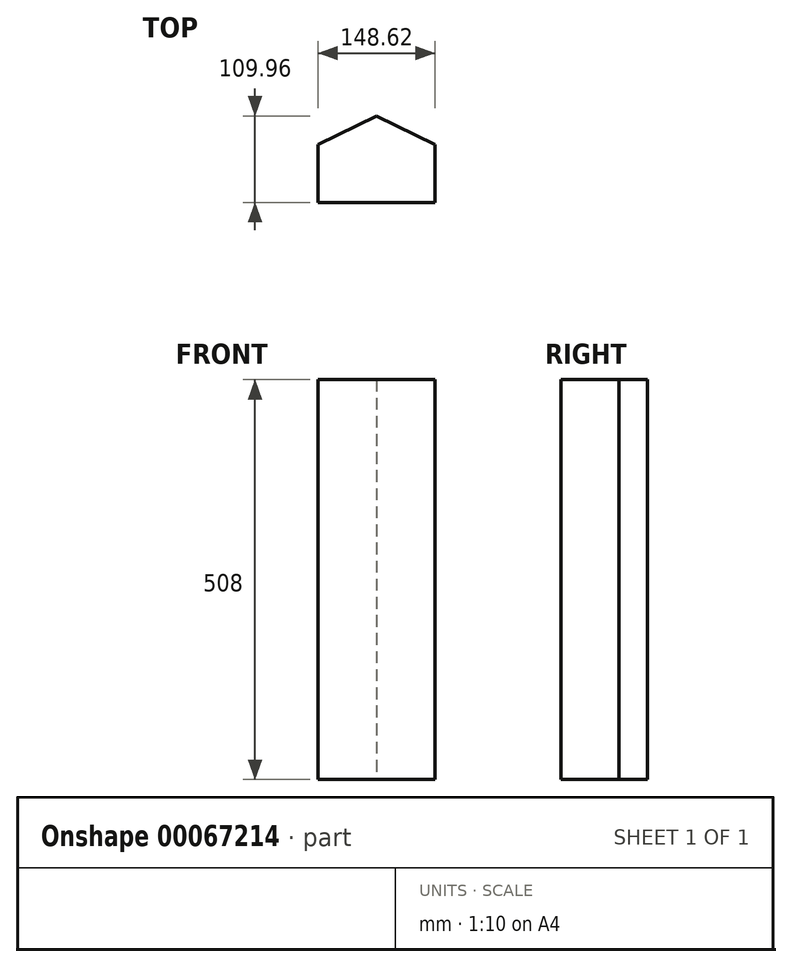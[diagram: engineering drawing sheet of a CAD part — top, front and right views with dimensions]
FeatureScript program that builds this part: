
annotation { "Feature Type Name" : "Feature", "Feature Type Description" : "" }
export const myFeature = defineFeature(function(context is Context, id is Id, definition is map)
    precondition{}
    {
        {
            var Q0;
            Q0=qCreatedBy(makeId("Top.planeOp"),FACE);
            var sketch = newSketch(context, id + "F0", { "sketchPlane" : qUnion([Q0])});
            skLineSegment(sketch, "E0.rect.bottom", {"start": v(0, -6) * mm, "end": v(0, -6) * mm});
            skLineSegment(sketch, "E0.rect.top", {"start": v(0, 6) * mm, "end": v(0, 6) * mm});
            skLineSegment(sketch, "E0.rect.left", {"start": v(0, -6) * mm, "end": v(0, 6) * mm});
            skLineSegment(sketch, "E0.rect.right", {"start": v(0, -6) * mm, "end": v(0, 6) * mm});
            skPoint(sketch, "E0.rect.middle", {"position": v(0, 0) * mm});
            skLineSegment(sketch, "E1.rect.bottom", {"start": v(-74.3, 36.85) * mm, "end": v(74.3, 36.85) * mm});
            skLineSegment(sketch, "E1.rect.top", {"start": v(-74.3, -36.85) * mm, "end": v(74.3, -36.85) * mm});
            skLineSegment(sketch, "E1.rect.left", {"start": v(-74.3, 36.85) * mm, "end": v(-74.3, -36.85) * mm});
            skLineSegment(sketch, "E1.rect.right", {"start": v(74.3, 36.85) * mm, "end": v(74.3, -36.85) * mm});
            skLineSegment(sketch, "E2", {"start": v(0, 73.1) * mm, "end": v(74.3, 36.85) * mm});
            skLineSegment(sketch, "E3", {"start": v(0, 73.1) * mm, "end": v(-74.3, 36.85) * mm});
            skSolve(sketch);
        }
        {
            var Q0;
            Q0 = qSketchRegion(id + "F0", true);
            extrude(context, id + "F1", {"entities" : qUnion([Q0]), "depth" : 508 * mm});
        }
    });
